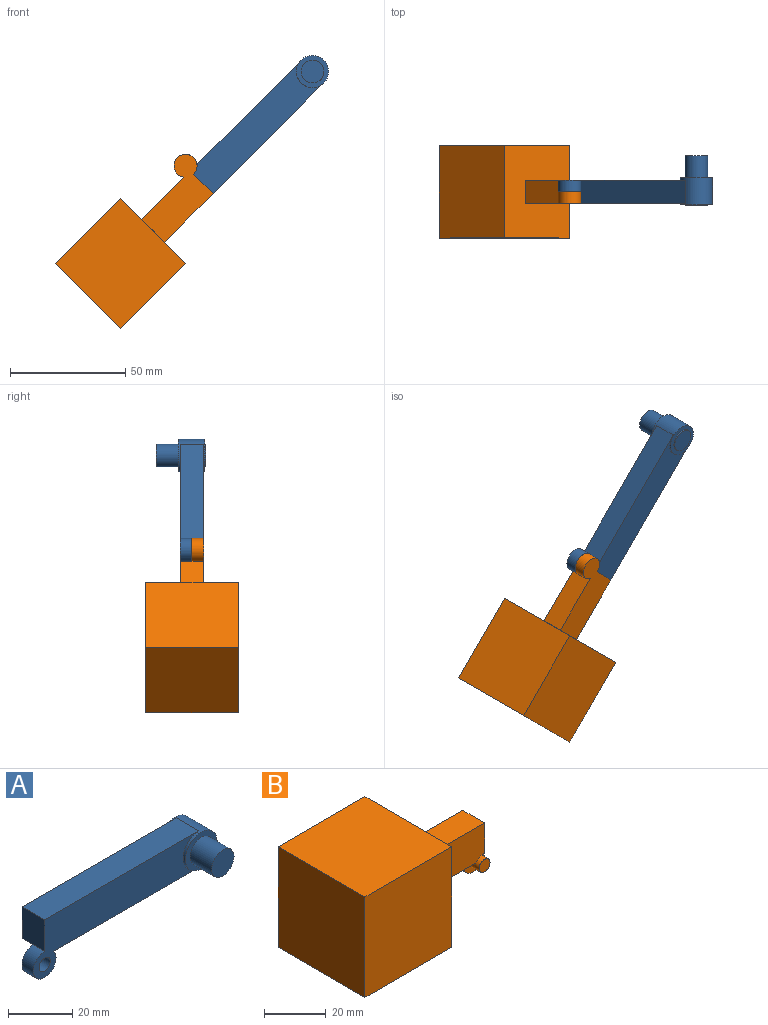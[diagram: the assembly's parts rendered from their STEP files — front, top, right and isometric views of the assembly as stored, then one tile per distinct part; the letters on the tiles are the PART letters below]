
ASSEMBLY  parts=2 mates=1
PART A: 16 faces, bbox 80x21.5x22 mm
  f0: cylinder r=5mm len=10mm, axis (0,1,0), area 133.9mm2, adj f2,f3,f4,f5
  f1: cylinder r=2.5mm len=5mm, axis (0,1,0), area 78.5mm2, adj f2,f3
  f2: plane 73x22mm, normal (0,-1,0), area 928.3mm2, adj f0,f1,f4,f5,f7,f9
  f3: plane 10x10mm, normal (0,1,0), area 58.9mm2, adj f0,f1,f6
  f4: plane 12x10mm, normal (-1,0,0), area 120mm2, adj f0,f2,f6,f7,f8
  f5: plane 64x10mm, normal (0,0,-1), area 640mm2, adj f0,f2,f6,f8,f9
  f6: cylinder r=5mm len=5mm, axis (0,1,0), area 23.2mm2, adj f3,f4,f5,f8
  f7: plane 68x10mm, normal (0,0,1), area 680mm2, adj f2,f4,f8,f9
  f8: plane 68x14mm, normal (0,1,0), area 869.4mm2, adj f4,f5,f6,f7,f9
  f9: cylinder r=7mm len=14mm, axis (0,1,0), area 285.9mm2, adj f2,f5,f7,f8,f10,f11
  f10: plane 14x14mm, normal (0,-1,0), area 77mm2, adj f9,f14
  f11: plane 14x14mm, normal (0,1,0), area 77mm2, adj f9,f13
  f12: plane 9.9x9.9mm, normal (0,1,0), area 77mm2, adj f13
  f13: cylinder r=4.95mm len=9.9mm, axis (0,-1,0), area 15.6mm2, adj f11,f12
  f14: cylinder r=4.95mm len=9.9mm, axis (0,-1,0), area 295.5mm2, adj f10,f15
  f15: plane 9.9x9.9mm, normal (0,-1,0), area 77mm2, adj f14
PART B: 16 faces, bbox 75x40x40 mm
  f0: cylinder r=5mm len=5mm, axis (0,1,0), area 23.2mm2, adj f1,f3,f4,f7
  f1: plane 12x10mm, normal (1,0,0), area 120mm2, adj f0,f2,f4,f5,f6
  f2: plane 30x10mm, normal (0,0,1), area 300mm2, adj f1,f4,f5,f10
  f3: plane 26x10mm, normal (0,0,-1), area 260mm2, adj f0,f4,f5,f6,f10
  f4: plane 30x14mm, normal (0,-1,0), area 414.4mm2, adj f0,f1,f2,f3,f10
  f5: plane 35x22mm, normal (0,1,0), area 492.9mm2, adj f1,f2,f3,f6,f10
  f6: cylinder r=5mm len=10mm, axis (0,-1,0), area 133.9mm2, adj f1,f3,f5,f7
  f7: plane 10x10mm, normal (0,-1,0), area 58.9mm2, adj f0,f6,f9
  f8: plane 5x5mm, normal (0,-1,0), area 19.6mm2, adj f9
  f9: cylinder r=2.5mm len=5mm, axis (0,1,0), area 78.5mm2, adj f7,f8
  f10: plane 40x40mm, normal (1,0,0), area 1460mm2, adj f2,f3,f4,f5,f11,f13,f14,f15
  f11: plane 40x40mm, normal (0,0,1), area 1600mm2, adj f10,f12,f14,f15
  f12: plane 40x40mm, normal (-1,0,0), area 1600mm2, adj f11,f13,f14,f15
  f13: plane 40x40mm, normal (0,0,-1), area 1600mm2, adj f10,f12,f14,f15
  f14: plane 40x40mm, normal (0,-1,0), area 1600mm2, adj f10,f11,f12,f13
  f15: plane 40x40mm, normal (0,1,0), area 1600mm2, adj f10,f11,f12,f13
PLACE A rot(axis=(0.92,0,0.38),180deg) t=(-3.05,-10.93,10.11)mm
PLACE B rot(axis=(0.92,0,0.38),180deg) t=(24.01,-10.93,37.17)mm
MATE revolute B.f0 <-> A.f0  axis (0,1,0) through (-20.83,-5.93,6.47)mm
